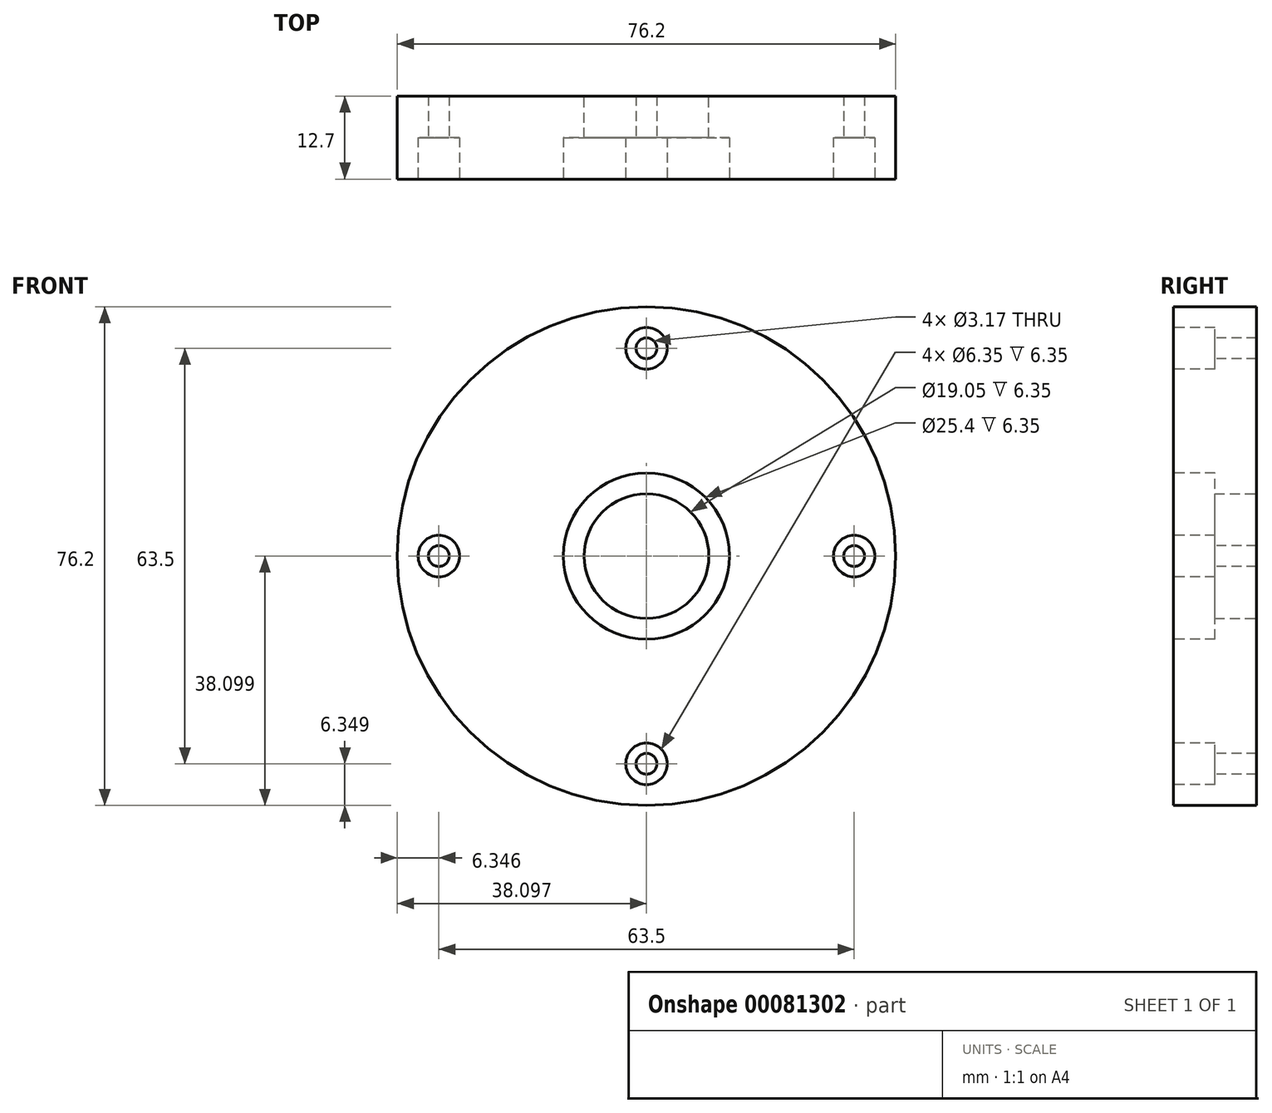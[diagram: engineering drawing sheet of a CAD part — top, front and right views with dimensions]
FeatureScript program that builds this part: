
annotation { "Feature Type Name" : "Feature", "Feature Type Description" : "" }
export const myFeature = defineFeature(function(context is Context, id is Id, definition is map)
    precondition{}
    {
        {
            var Q0;
            Q0=qCreatedBy(makeId("Front.planeOp"),FACE);
            var sketch = newSketch(context, id + "F0", { "sketchPlane" : qUnion([Q0])});
            skCircle(sketch, "E0", {"center": v(-20.07, 16.95) * mm, "radius": 38.1 * mm});
            skCircle(sketch, "E1", {"center": v(-20.07, 16.95) * mm, "radius": 9.53 * mm});
            skSolve(sketch);
        }
        {
            var Q0;
            Q0=makeQuery(id+"F0.imprint","IMPRINT",FACE,{"disambiguationData":[TD([[makeQuery(id+"F0.imprint","IMPRINT",EDGE,{"derivedFrom":sQuery(id+"F0.wireOp",EDGE,"E0")}),1.0]])]});
            extrude(context, id + "F1", {"entities" : qUnion([Q0]), "depth" : 12.7 * mm});
        }
        {
            var Q0;
            Q0=makeQuery(id+"F1.opExtrude","CAP_FACE",FACE,{"disambiguationData":[OSD([sQuery(id+"F0.wireOp",EDGE,"E0"),sQuery(id+"F0.wireOp",EDGE,"E1")])],"isStart":false});
            var sketch = newSketch(context, id + "F2", { "sketchPlane" : qUnion([Q0])});
            skCircle(sketch, "E2", {"center": v(-20.07, 16.95) * mm, "radius": 12.7 * mm});
            skSolve(sketch);
        }
        {
            var Q0;
            Q0 = qSketchRegion(id + "F2", true);
            extrude(context, id + "F3", {"entities" : qUnion([Q0]), "operationType" : NewBodyOperationType.REMOVE, "oppositeDirection" : true, "depth" : 6.35 * mm});
        }
        {
            var Q0;
            Q0=makeQuery(id+"F1.opExtrude","CAP_FACE",FACE,{"disambiguationData":[OSD([sQuery(id+"F0.wireOp",EDGE,"E0"),sQuery(id+"F0.wireOp",EDGE,"E1")])],"isStart":false});
            var sketch = newSketch(context, id + "F4", { "sketchPlane" : qUnion([Q0])});
            skPoint(sketch, "E3", {"position": v(11.68, 16.95) * mm});
            skPoint(sketch, "E4", {"position": v(-20.07, 48.7) * mm});
            skPoint(sketch, "E5", {"position": v(-51.82, 16.95) * mm});
            skPoint(sketch, "E6", {"position": v(-20.07, -14.8) * mm});
            skCircle(sketch, "E7.0", {"center": v(-20.07, 16.95) * mm, "radius": 12.7 * mm});
            skSolve(sketch);
        }
        {
            var Q0;
            Q0=sQuery(id+"F4.wireOp",VERTEX,"E4");
            var Q1;
            Q1=sQuery(id+"F4.wireOp",VERTEX,"E5");
            var Q2;
            Q2=sQuery(id+"F4.wireOp",VERTEX,"E6");
            var Q3;
            Q3=sQuery(id+"F4.wireOp",VERTEX,"E3");
            var Q4;
            Q4=makeQuery(id+"F1.opExtrude","SWEPT_BODY",BODY,{"disambiguationData":[OSD([sQuery(id+"F0.wireOp",EDGE,"E0"),sQuery(id+"F0.wireOp",EDGE,"E1")])]});
            hole(context, id + "F5", {"style" : HoleStyle.C_BORE, "endStyle" : HoleEndStyle.THROUGH, "holeDiameter" : 3.17 * mm, "cBoreDiameter" : 6.35 * mm, "cBoreDepth" : 6.35 * mm, "locations" : qUnion([Q0, Q1, Q2, Q3]), "scope" : qUnion([Q4]), "isTappedThrough" : true});
        }
    });
